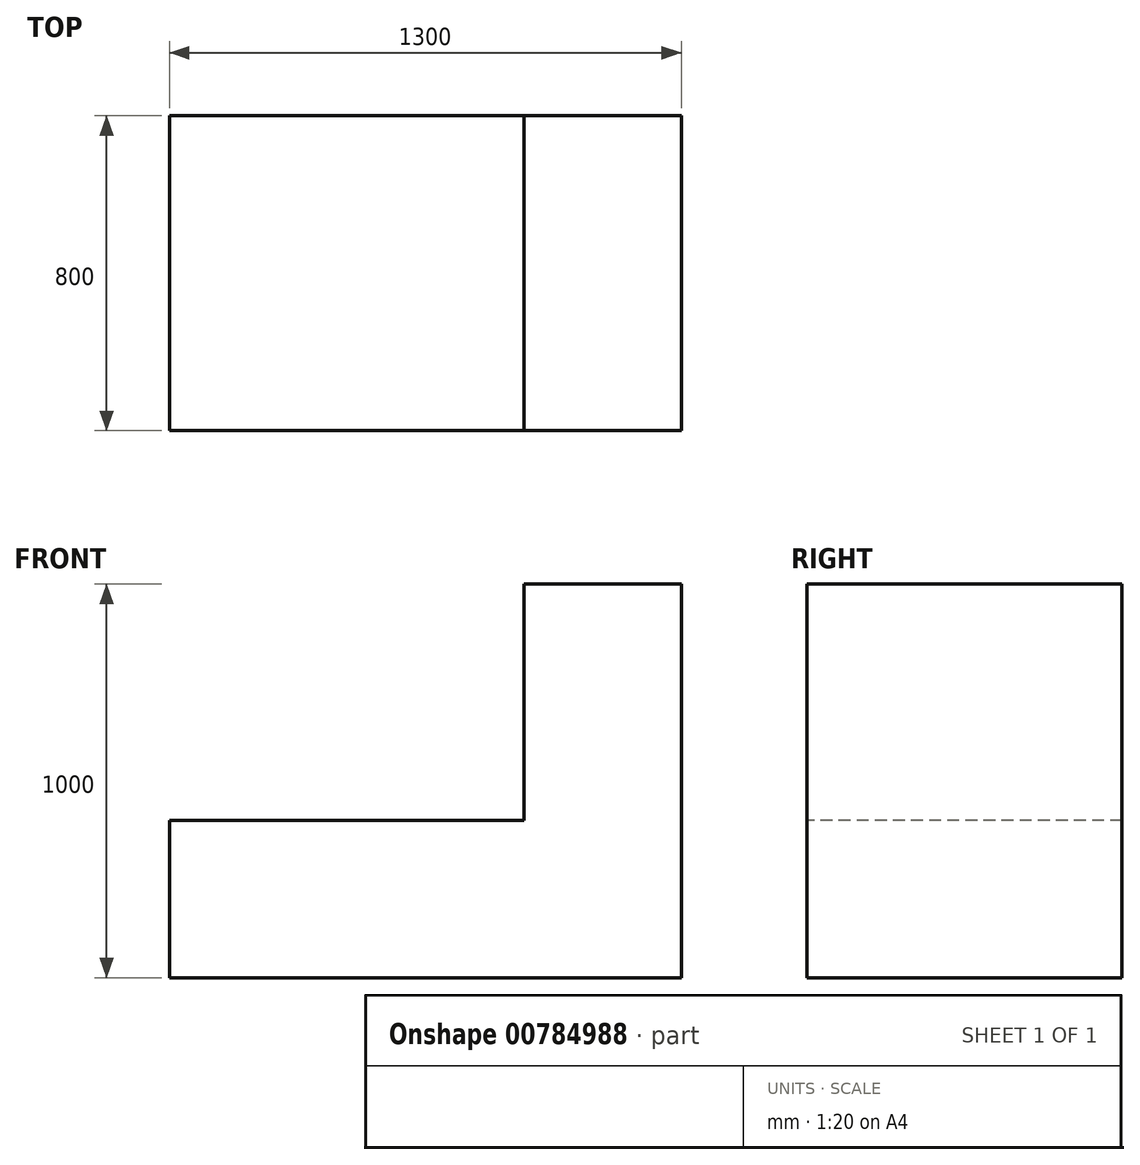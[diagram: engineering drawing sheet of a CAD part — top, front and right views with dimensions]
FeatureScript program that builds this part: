
annotation { "Feature Type Name" : "Feature", "Feature Type Description" : "" }
export const myFeature = defineFeature(function(context is Context, id is Id, definition is map)
    precondition{}
    {
        {
            var Q0;
            Q0=qCreatedBy(makeId("Top.planeOp"),FACE);
            var sketch = newSketch(context, id + "F0", { "sketchPlane" : qUnion([Q0])});
            skLineSegment(sketch, "E0.bottom", {"start": v(-472.58, 500.15) * mm, "end": v(427.42, 500.15) * mm});
            skLineSegment(sketch, "E0.top", {"start": v(-472.58, -299.85) * mm, "end": v(427.42, -299.85) * mm});
            skLineSegment(sketch, "E0.left", {"start": v(-472.58, 500.15) * mm, "end": v(-472.58, -299.85) * mm});
            skLineSegment(sketch, "E0.right", {"start": v(427.42, 500.15) * mm, "end": v(427.42, -299.85) * mm});
            skSolve(sketch);
        }
        {
            var Q0;
            Q0=makeQuery(id+"F0.imprint","IMPRINT",FACE,{"disambiguationData":[TD([[makeQuery(id+"F0.imprint","IMPRINT",EDGE,{"derivedFrom":sQuery(id+"F0.wireOp",EDGE,"E0.bottom")}),-1.0]])]});
            extrude(context, id + "F1", {"entities" : qUnion([Q0]), "oppositeDirection" : true, "depth" : 400 * mm, "offsetDistance" : 25 * mm});
        }
        {
            var Q0;
            Q0=makeQuery(id+"F1.opExtrude","CAP_FACE",FACE,{"disambiguationData":[OSD([sQuery(id+"F0.wireOp",EDGE,"E0.bottom"),sQuery(id+"F0.wireOp",EDGE,"E0.top"),sQuery(id+"F0.wireOp",EDGE,"E0.left"),sQuery(id+"F0.wireOp",EDGE,"E0.right")])],"isStart":false});
            var sketch = newSketch(context, id + "F2", { "sketchPlane" : qUnion([Q0])});
            skLineSegment(sketch, "E1.bottom", {"start": v(427.42, 299.85) * mm, "end": v(827.42, 299.85) * mm});
            skLineSegment(sketch, "E1.top", {"start": v(427.42, -500.15) * mm, "end": v(827.42, -500.15) * mm});
            skLineSegment(sketch, "E1.left", {"start": v(427.42, 299.85) * mm, "end": v(427.42, -500.15) * mm});
            skLineSegment(sketch, "E1.right", {"start": v(827.42, 299.85) * mm, "end": v(827.42, -500.15) * mm});
            skSolve(sketch);
        }
        {
            var Q0;
            Q0=makeQuery(id+"F2.imprint","IMPRINT",FACE,{"disambiguationData":[TD([[makeQuery(id+"F2.imprint","IMPRINT",EDGE,{"derivedFrom":sQuery(id+"F2.wireOp",EDGE,"E1.bottom")}),-1.0]])]});
            extrude(context, id + "F3", {"entities" : qUnion([Q0]), "operationType" : NewBodyOperationType.ADD, "oppositeDirection" : true, "depth" : 1000 * mm, "offsetDistance" : 25 * mm});
        }
    });
